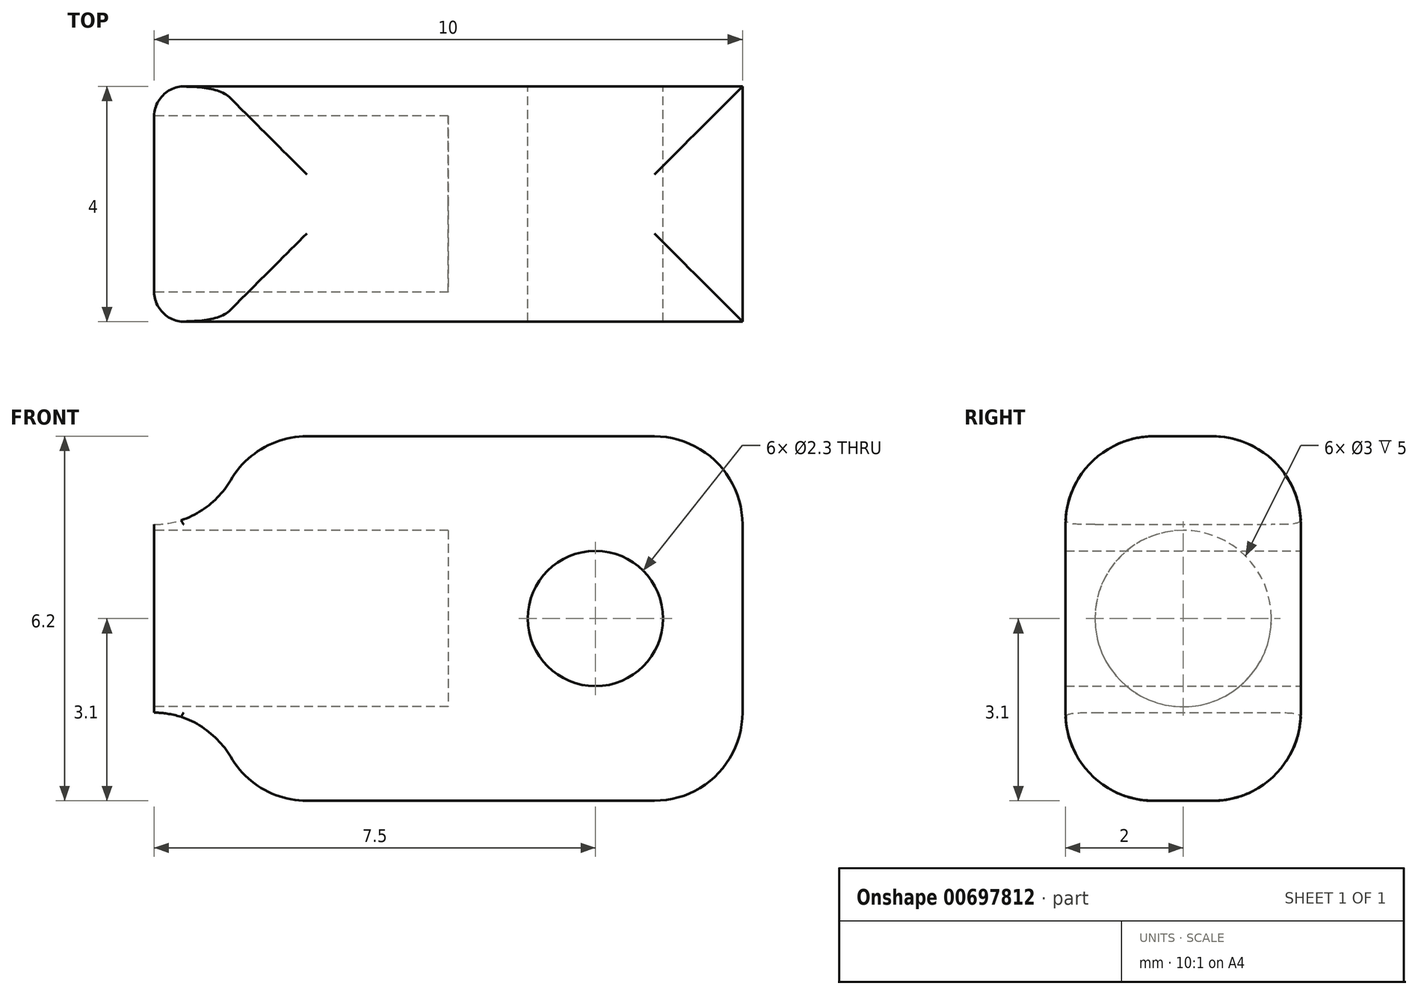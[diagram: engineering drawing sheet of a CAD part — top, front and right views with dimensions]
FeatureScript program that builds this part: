
annotation { "Feature Type Name" : "Feature", "Feature Type Description" : "" }
export const myFeature = defineFeature(function(context is Context, id is Id, definition is map)
    precondition{}
    {
        {
            var Q0;
            Q0=qCreatedBy(makeId("Front.planeOp"),FACE);
            var sketch = newSketch(context, id + "F0", { "sketchPlane" : qUnion([Q0])});
            skLineSegment(sketch, "E0.bottom", {"start": v(-3.5, 3.1) * mm, "end": v(5, 3.1) * mm});
            skLineSegment(sketch, "E0.top", {"start": v(-3.5, -3.1) * mm, "end": v(5, -3.1) * mm});
            skLineSegment(sketch, "E0.left", {"start": v(-5, 1.6) * mm, "end": v(-5, -1.6) * mm});
            skLineSegment(sketch, "E0.right", {"start": v(5, 3.1) * mm, "end": v(5, -3.1) * mm});
            skPoint(sketch, "E0.middle", {"position": v(0, 0) * mm});
            skArc(sketch, "E1", {"start": v(-5, 1.6) * mm, "mid": v(-3.94, 2.04) * mm, "end": v(-3.5, 3.1) * mm});
            skArc(sketch, "E2.MirrorCS", {"start": v(-5, -1.6) * mm, "mid": v(-3.94, -2.04) * mm, "end": v(-3.5, -3.1) * mm});
            skCircle(sketch, "E3", {"center": v(2.5, 0) * mm, "radius": 1.15 * mm});
            skSolve(sketch);
        }
        {
            var Q0;
            Q0=qSketchRegion(id+"F0",true);
            extrude(context, id + "F1", {"entities" : qUnion([Q0]), "depth" : 4 * mm, "offsetDistance" : 25 * mm, "symmetric" : true});
        }
        {
            var Q0;
            Q0=makeQuery(id+"F1.opExtrude","CAP_EDGE",EDGE,{"disambiguationData":[OSD([sQuery(id+"F0.wireOp",EDGE,"E0.bottom")])],"isStart":false});
            var Q1;
            Q1=makeQuery(id+"F1.opExtrude","SWEPT_FACE",FACE,{"disambiguationData":[OSD([sQuery(id+"F0.wireOp",EDGE,"E0.bottom")])]});
            var Q2;
            Q2=makeQuery(id+"F1.opExtrude","SWEPT_FACE",FACE,{"disambiguationData":[OSD([sQuery(id+"F0.wireOp",EDGE,"E0.top")])]});
            fillet(context, id + "F2", {"entities" : qUnion([Q0, Q1, Q2]), "radius" : 1.5 * mm, "tangentPropagation" : true, "allowEdgeOverflow" : false});
        }
        {
            var Q0;
            Q0=makeQuery(id+"F1.opExtrude","SWEPT_FACE",FACE,{"disambiguationData":[OSD([sQuery(id+"F0.wireOp",EDGE,"E0.left")])]});
            var sketch = newSketch(context, id + "F3", { "sketchPlane" : qUnion([Q0])});
            skCircle(sketch, "E4", {"center": v(0, 0) * mm, "radius": 1.5 * mm});
            skSolve(sketch);
        }
        {
            var Q0;
            Q0=makeQuery(id+"F1.opExtrude","CAP_EDGE",EDGE,{"disambiguationData":[OSD([sQuery(id+"F0.wireOp",EDGE,"E0.left")])],"isStart":false});
            var Q1;
            Q1=makeQuery(id+"F1.opExtrude","CAP_EDGE",EDGE,{"disambiguationData":[OSD([sQuery(id+"F0.wireOp",EDGE,"E0.left")])],"isStart":true});
            fillet(context, id + "F4", {"entities" : qUnion([Q0, Q1]), "radius" : .5 * mm, "tangentPropagation" : true, "allowEdgeOverflow" : false});
        }
        {
            var Q0;
            Q0=makeQuery(id+"F3.imprint","IMPRINT",FACE,{"disambiguationData":[TD([[makeQuery(id+"F3.imprint","IMPRINT",EDGE,{"derivedFrom":sQuery(id+"F3.wireOp",EDGE,"E4")}),1.0]])]});
            extrude(context, id + "F5", {"entities" : qUnion([Q0]), "operationType" : NewBodyOperationType.REMOVE, "oppositeDirection" : true, "depth" : 5 * mm, "offsetDistance" : 25 * mm});
        }
    });
